# Revit family: hpd2_033200
name_source: partatom
category: Elektroinstallationen
revit_build: Autodesk Revit 2016 (Build: 20190508_0715(x64)
units: mm (PartAtom-declared; Revit-internal decimal feet)

## family parameters
Basisbauteil = Fläche
Beim Laden mit Abzugskörper schneiden = Nein
Bemaßung runder Anschluss = Durchmesser verwenden
Beschriftungsausrichtung beibehalten = Nein
Gemeinsam genutzt = Nein
Raumberechnungspunkt = Nein
Teiletyp = Normal

## types (1)
- HPD2
    Apparent Load = 0 VA
    Beschreibung = Type: Other; Dimensions (L x W x H): 52 x 86 x 156 mm; Mains power supply: 21.0 – 30 V; Power supply, detail: KNX bus, additional voltage of 18-57 V DC, 130 mA bus current; Sensor Technology: Optical sensor; Application, place: Indoors; Application, room: classroom, lecture hall, open-plan office, production facilities, conference room / meeting room, recreation room, Indoors; Installation site: wall, corner; Installation: Surface wiring; Switching zones: 5 switching zones; Electronic scalability: Yes; Mounting height: 2,3 – 6,0 m; Optimum mounting height: 2,8 m; Detection angle: 110 °; Angle of aperture: 110 °; Sneak-by guard: Yes; Reach, radial: r = 10 m (96 m²); Reach, tangential: r = 10 m (96 m²); Reach, presence: r = 10 m (96 m²); Twilight setting TEACH: No; Time setting: 1 sec – 255 min; Constant-lighting control: Yes; Basic light level function: Yes; KNX functions: Light level, Humidity output, Presence output, Temperature output; With bus coupling: Yes; Settings via: ETS software, Web-Interface; With remote control: No; IP-rating: IP20; Material: Plastic; Ambient temperature: 0 – 40 °C; Colour: white; Colour, RAL: 9010; Manufacturer's Warranty: 5 years; Version: KNX; PU1, EAN: 4007841033200
    Height = 156 mm  [stored 0.511811 ft]
    Hersteller = Steinel
    Length = 52 mm  [stored 0.170604 ft]
    Maximum range = 15.292 m
    ModVariant = Nein
    Modell = 033200
    Mounting Type = Surface mounted
    Number of Poles = 1
    OnlyDefault = Ja
    Power Factor = 1
    Product Name = HPD2
    Product group = Sensor-switched indoor light
    ProductGroupID = 30
    Protection Class = Safety extra-low voltage
    Protection Degree = IP 20
    RlxData = <blob elided: 146797 chars, md5=7cb1325f>
    Sensor characteristics = Sector <145°
    Sensor type = Passive (infrared)
    SensorDataFile = <blob elided: 92443 chars, md5=e855ff4b>
    Type of entry = Presence, Motion
    Typenbild = produkt1_033200.jpg
    Typenkommentare = Product without accessories
    URL = http://relux.com
    VarID = ---
    Voltage = 0 V
    Vorgabe-Ansicht = 1800 mm
    Weight = 0.00 kg
    Width = 86 mm

note: [stored X ft] marks values corroborated as IEEE doubles in the binary element streams (Revit-internal decimal feet)

## geometry (parser evidence)
native form markers: Blend x4, Sweep x21
no freeform markers — native parametric forms only
